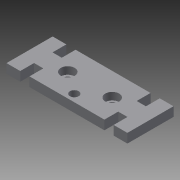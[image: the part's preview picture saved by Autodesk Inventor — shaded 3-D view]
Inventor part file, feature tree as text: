
AUTODESK INVENTOR PART (.ipt)
format: ipt  version: 2015 (Build 190159000, 159)  size: 122,368 bytes
history: native  units: mm
features: extrude x4, sketch x3
ambient origin geometry x8: Origin, YZ Plane, XZ Plane, XY Plane, X Axis, Y Axis, Z Axis, Center Point
bodies: Body1 (feature_tree)
feature tree (7):
  sketch  "Sketch1"  dims[d0=15.0mm d1=15.0mm d2=15.0mm d3=15.0mm d8=15.0mm]
  extrude  "Extrusion2"  Depth=15.0mm
  extrude  "Extrusion3"  Depth=10.0mm TaperAngle=0.0deg
  sketch  "Sketch3"  dims[d15=2.5mm d16=2.5mm d17=10.0mm d18=0.0mm d25=48.2mm d35=8.0mm d36=9.5mm d37=10.0mm d38=0.0mm d39=10.0mm d40=10.0mm d41=2.0mm d42=0.0mm]
  extrude  "Extrusion8"  Depth=2.0mm
  extrude  "Extrusion9"  Depth=10.0mm TaperAngle=0.0deg
  sketch  "Sketch2"  dims[d9=15.0mm d10=10.0mm d11=0.0mm]
